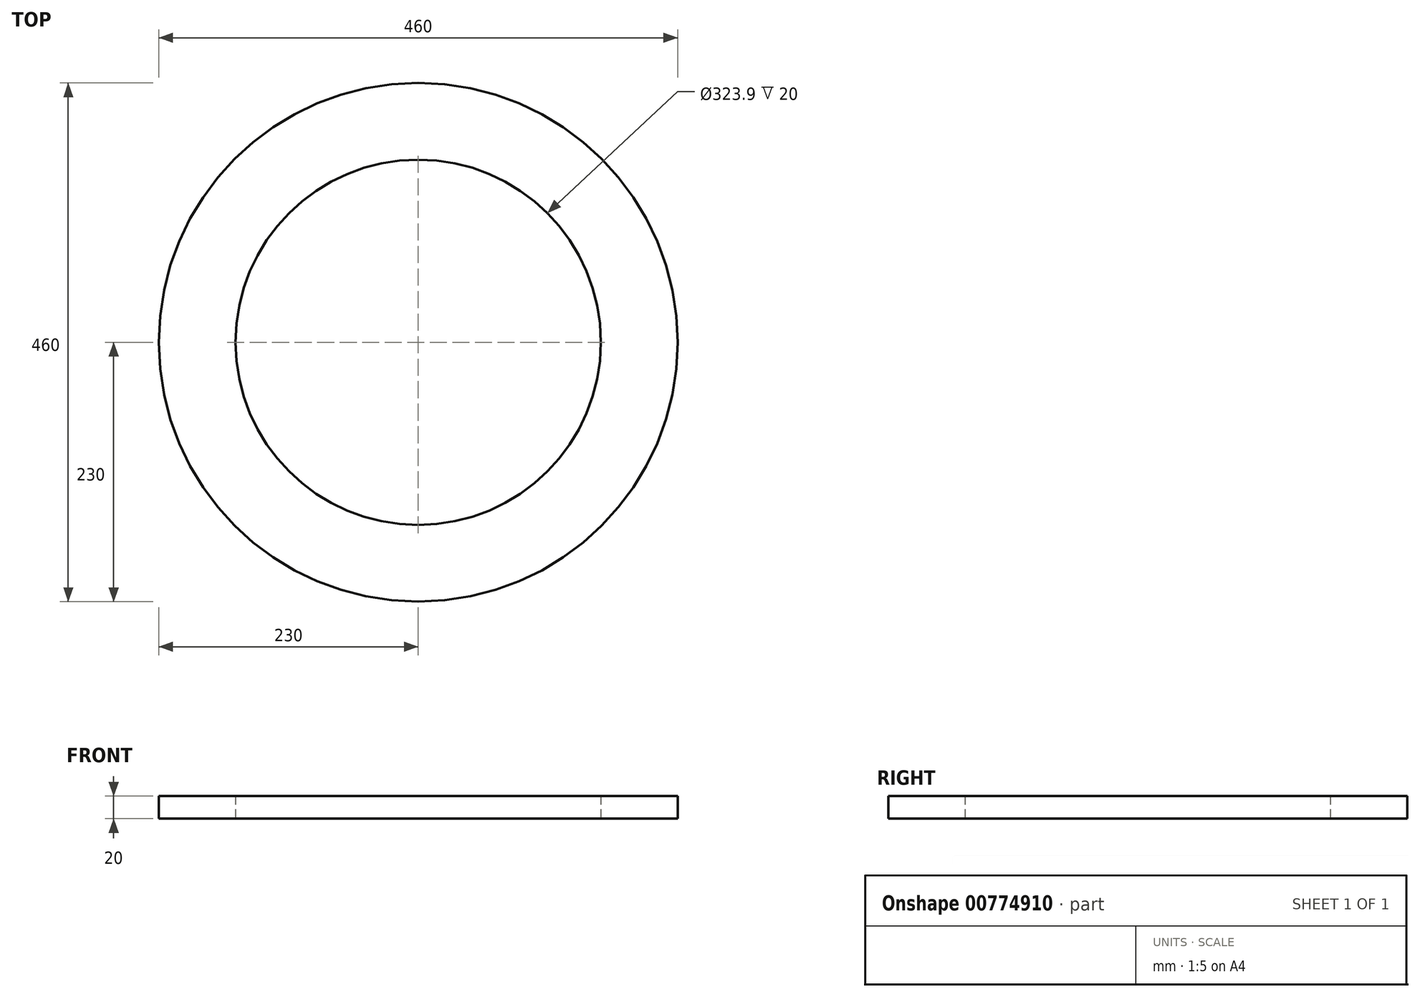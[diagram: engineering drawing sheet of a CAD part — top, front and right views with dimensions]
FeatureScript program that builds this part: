
annotation { "Feature Type Name" : "Feature", "Feature Type Description" : "" }
export const myFeature = defineFeature(function(context is Context, id is Id, definition is map)
    precondition{}
    {
        {
            var Q0;
            Q0=qCreatedBy(makeId("Top.planeOp"),FACE);
            var sketch = newSketch(context, id + "F0", { "sketchPlane" : qUnion([Q0])});
            skCircle(sketch, "E0", {"center": v(0, 0) * mm, "radius": 230 * mm});
            skCircle(sketch, "E1", {"center": v(0, 0) * mm, "radius": 161.95 * mm});
            skSolve(sketch);
        }
        {
            var Q0;
            Q0=makeQuery(id+"F0.imprint","IMPRINT",FACE,{"disambiguationData":[TD([[makeQuery(id+"F0.imprint","IMPRINT",EDGE,{"derivedFrom":sQuery(id+"F0.wireOp",EDGE,"E0")}),1.0]])]});
            extrude(context, id + "F1", {"entities" : qUnion([Q0]), "depth" : 20 * mm, "offsetDistance" : 25 * mm});
        }
    });
